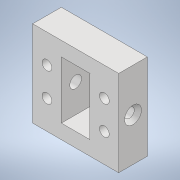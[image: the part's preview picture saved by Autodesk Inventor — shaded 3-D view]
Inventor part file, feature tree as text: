
AUTODESK INVENTOR PART (.ipt)
format: ipt  version: 2022.3 (Build 263350000, 350)  size: 205,312 bytes
history: native  units: mm
features: sketch x5, hole x3, extrude x2, fillet x2
ambient origin geometry x8: Origin, YZ Plane, XZ Plane, XY Plane, X Axis, Y Axis, Z Axis, Center Point
bodies: Solid1 (feature_tree)
feature tree (12):
  extrude  "Extrusion1"  Depth=10.0mm
  extrude  "Extrusion2"  Depth=10.0mm
  hole  "Hole1"  [1 undecoded]
  hole  "Hole2"  [1 undecoded]
  hole  "Hole3"  [1 undecoded]
  fillet  "Fillet1"  Radius=10.0mm
  fillet  "Fillet2"  Radius=6.0mm
  sketch  "Sketch1"  dims[d0=30.0mm d1=10.0mm]
  sketch  "Sketch2"  dims[d2=30.0mm d3=0.0mm d4=10.0mm]
  sketch  "Sketch3"  dims[d5=20.0mm d6=0.0mm d7=0.0mm]
  sketch  "Sketch4"  dims[d8=3.4mm d9=6.0mm d10=5.9mm d11=2.0mm d12=90.0deg d13=10.0mm d14=0.0mm d15=10.0mm]
  sketch  "Sketch5"  dims[d16=3.4mm d17=6.0mm d18=4.1mm d19=5.1mm d20=90.0deg d21=3.9mm d22=0.0mm d23=20.0mm d24=10.0mm d25=3.4mm d26=6.0mm d27=5.9mm d28=2.0mm d29=90.0deg d30=8.0mm d31=0.0mm d32=6.0mm d33=2.0mm]
note: 3 required parameter values undecoded (feature->parameter linkage not recoverable at this tier; creation-order binding heuristic only, values carry confidence <= 0.55)
